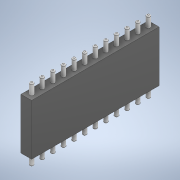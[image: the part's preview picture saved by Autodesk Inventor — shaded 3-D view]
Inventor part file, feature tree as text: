
AUTODESK INVENTOR PART (.ipt)
format: ipt  version: 2021 (Build 250183000, 183)  size: 157,184 bytes
history: native  units: in
note: dims shown in document units (in); Inventor stores cm internally (conversion verified against a paired STEP export)
features: extrude x2, sketch x2, fillet x1, pattern_linear x1, plane x1, mirror x1
ambient origin geometry x8: Origin, YZ Plane, XZ Plane, XY Plane, X Axis, Y Axis, Z Axis, Center Point
bodies: Solid1 (feature_tree)
feature tree (8):
  extrude  "Extrusion1"  Depth=0.1in
  extrude  "Extrusion2"  Depth=0.1in
  fillet  "Fillet1"  Radius=0.05in
  pattern_linear  "Rectangular Pattern1"  Spacing1=0.05in  [1 undecoded]
  plane  "Work Plane1"
  mirror  "Mirror1"
  sketch  "Sketch1"  dims[d0=1.2in d1=0.1in]
  sketch  "Sketch2"  dims[d2=0.48in d3=0.0in d4=0.0354in d5=0.05in d6=0.05in d7=0.1in d8=0.0in d9=0.01in d10=4.7244in d12=0.1in]
note: 1 required parameter value undecoded (feature->parameter linkage not recoverable at this tier; creation-order binding heuristic only, values carry confidence <= 0.55)
